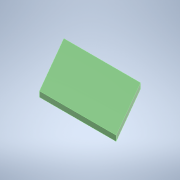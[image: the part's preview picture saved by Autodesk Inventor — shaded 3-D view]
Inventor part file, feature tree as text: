
AUTODESK INVENTOR PART (.ipt)
format: ipt  version: 2021 (Build 250183000, 183)  size: 110,592 bytes
history: native  units: mm
features: extrude x1, sketch x1
ambient origin geometry x8: Origin, YZ Plane, XZ Plane, XY Plane, X Axis, Y Axis, Z Axis, Center Point
bodies: Solid1 (feature_tree)
feature tree (2):
  extrude  "Extrusion1"  Depth=20.15mm
  sketch  "Sketch1"  dims[d10=1.9mm d11=0.0mm d12=20.15mm d13=120.0deg d14=23.2mm]
